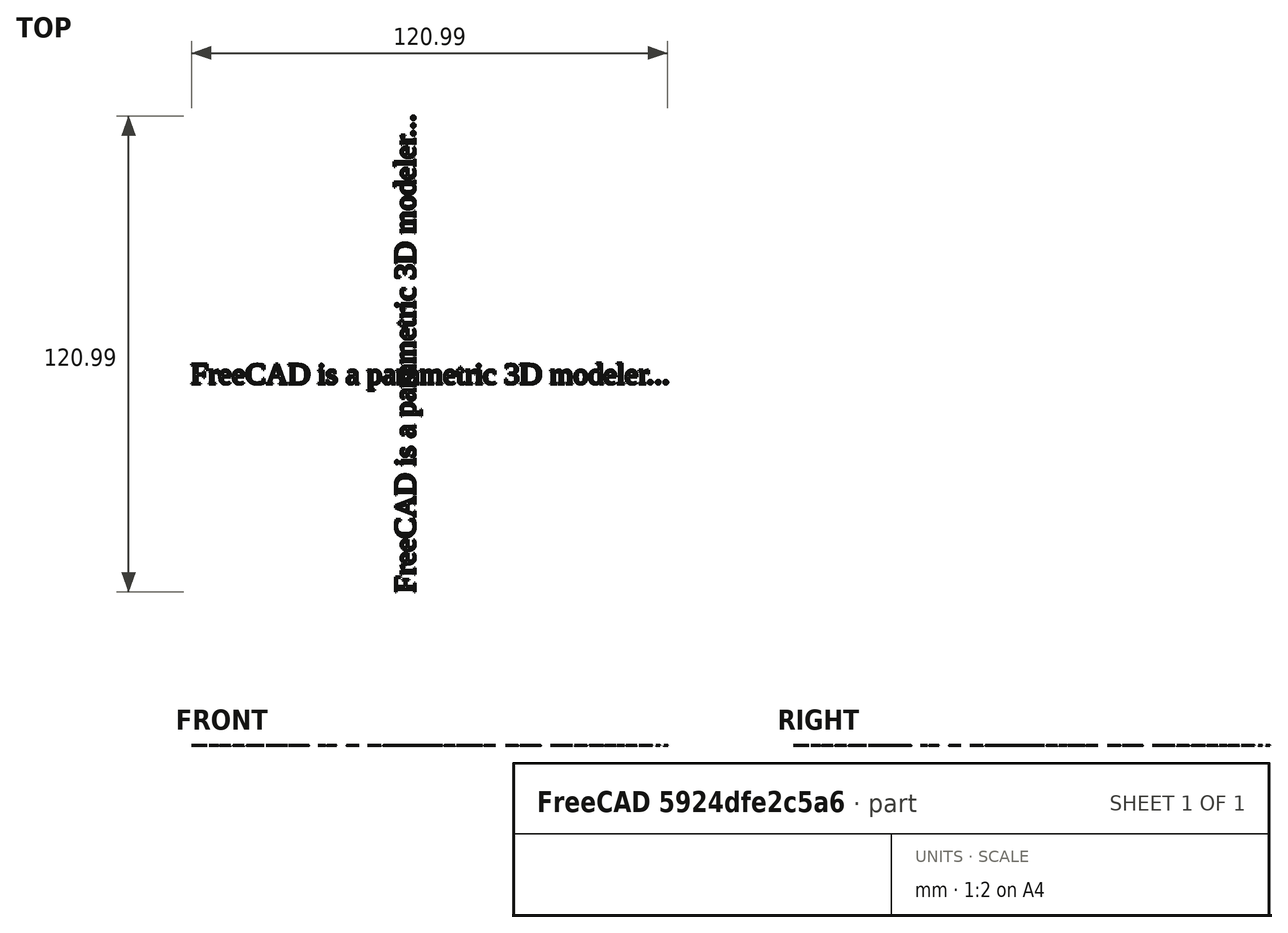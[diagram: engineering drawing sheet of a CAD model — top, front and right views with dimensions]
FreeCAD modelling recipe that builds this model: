
FCSTD DOCUMENT  (FreeCAD 0.17R13327 (Git))
Label: engraving
License: All rights reserved
LicenseURL: http://en.wikipedia.org/wiki/All_rights_reserved
objects: Part::Part2DObjectPython×1, Sketcher::SketchObject×1, Part::FeaturePython×1
note: 3 computed .brp shape members not serialized (recipe doc carries the construction recipe); baked Part::Feature solids carry a one-line shape summary decoded from their .brp

FEATURE [Part::Part2DObjectPython] ShapeString  # Draft 2D object (typed FeaturePython)
  FontFile = <path>
  Placement = pos=(-55,-2,0) rot=(0,0,1;0rad)
  Size = 6
  String = FreeCAD is a parametric 3D modeler...
  Tracking = 0
FEATURE [Sketcher::SketchObject] Sketch
  sketch-geometry (8):
    g0: LineSegment StartX=-60.4214 StartY=99.4938 StartZ=0 EndX=-104.979 EndY=37.1095 EndZ=0
    g1: LineSegment StartX=-104.979 StartY=37.1095 StartZ=0 EndX=-73.5312 EndY=34.5247 EndZ=0
    g2: LineSegment StartX=-73.5312 StartY=34.5247 StartZ=0 EndX=-61.8996 EndY=50.8951 EndZ=0
    g3: LineSegment StartX=-61.8996 StartY=50.8951 StartZ=0 EndX=-55.4376 EndY=33.6632 EndZ=0
    g4: ArcOfCircle CenterX=-48.335 CenterY=36.3266 CenterZ=0 NormalX=0 NormalY=0 NormalZ=1 AngleXU=0 Radius=7.58559 StartAngle=3.50036 EndAngle=7.28324
    g5: LineSegment StartX=-44.2369 StartY=42.7099 StartZ=0 EndX=-36.9133 EndY=72.8658 EndZ=0
    g6: ArcOfCircle CenterX=-35.2504 CenterY=79.7128 CenterZ=0 NormalX=0 NormalY=0 NormalZ=1 AngleXU=0 Radius=7.04606 StartAngle=2.47553 EndAngle=4.47414
    g7: LineSegment StartX=-40.7905 StartY=84.0666 StartZ=0 EndX=-60.4214 EndY=99.4938 EndZ=0
  constraints (8):
    c: Coincident(g0,g1)
    c: Coincident(g1,g2)
    c: Coincident(g2,g3)
    c: Tangent(g3,g4) = -1.5708
    c: Coincident(g4,g5)
    c: Perpendicular(g5,g6) = 4.71239
    c: Perpendicular(g6,g7) = 4.71239
    c: Coincident(g7,g0)
FEATURE [Part::FeaturePython] Array  # Draft array (typed FeaturePython)
  Angle = 90
  ArrayType = 1
  Axis = (0,0,1)
  Base = -> ShapeString
  Center = (0,0,0)
  Fuse = false
  IntervalAxis = (0,0,0)
  IntervalX = (1,0,0)
  IntervalY = (0,1,0)
  IntervalZ = (0,0,0)
  NumberPolar = 2
  NumberX = 2
  NumberY = 2
  NumberZ = 1
note: 1 file-system path scrubbed to <path> (originals preserved in the JSON sidecar)
